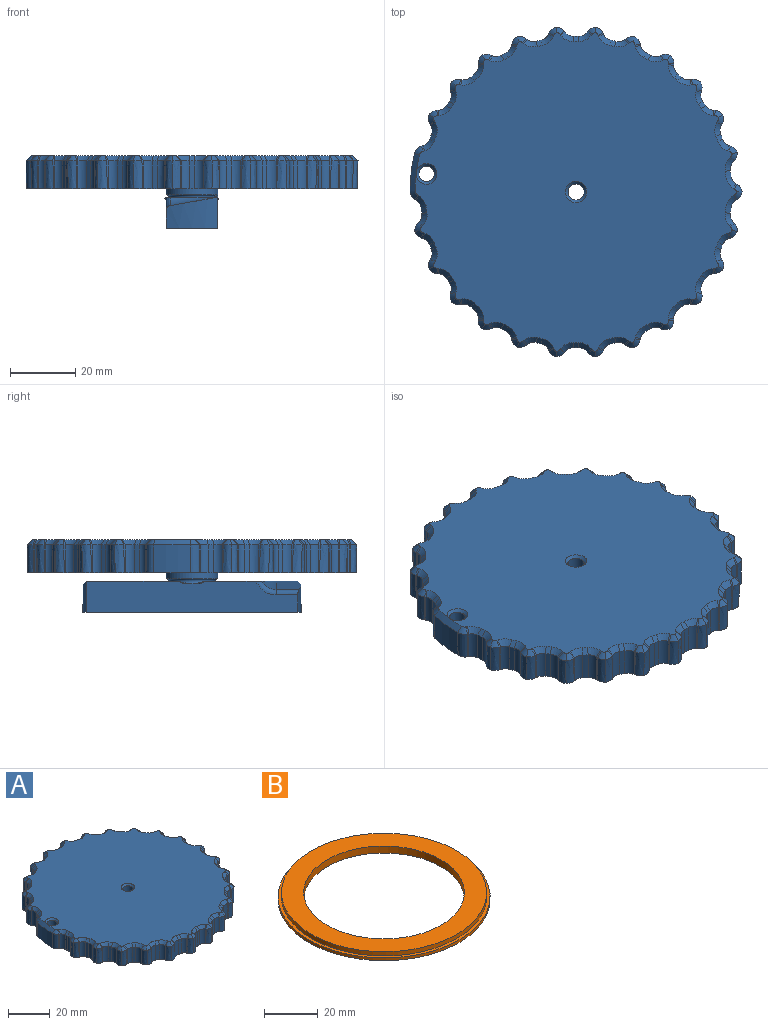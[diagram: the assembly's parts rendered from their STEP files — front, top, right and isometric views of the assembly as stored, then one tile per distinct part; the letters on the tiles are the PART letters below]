
ASSEMBLY  parts=2 mates=1
PART A: 388 faces, bbox 105.4x104.9x57.9 mm
  f0: plane 66.68x15.88mm, normal (0,0,-1), area 971.9mm2, adj f4,f5,f6,f15,f374,f375,f376,f377
  f1: plane 98.34x97.56mm, normal (0,0,1), area 6895.4mm2, adj f195,f196,f197,f198,f199,f200,f201,f202
  f2: cone r=50.8mm half-angle=0.9deg, axis (0,0,1), area 98.1mm2, adj f3,f117,f118,f370
  f3: cone r=50.64mm half-angle=89.1deg, axis (0,0,-1), area 1716.2mm2, adj f2,f13,f20,f21,f22,f23,f24,f25
  f4: cylinder r=33.34mm len=15.88mm, axis (0,0,-1), area 129.3mm2, adj f0,f5,f15,f17,f386
  f5: plane 65.7x10.47mm, normal (-1,0,0), area 566mm2, adj f0,f4,f6,f7,f8,f9,f17,f384
  f6: cylinder r=33.34mm len=15.88mm, axis (0,0,-1), area 129.3mm2, adj f0,f5,f15,f16,f384
  f7: torus R=7.94mm, axis (0,0,-1), area 187.3mm2, adj f5,f8,f9,f12,f15
  f8: plane 25.26x19.05mm, normal (0,0,1), area 240.7mm2, adj f5,f7,f15,f19,f385
  f9: plane 22.28x16.07mm, normal (0,0,1), area 240.7mm2, adj f5,f7,f15,f18,f387
  f10: plane 76.2x76.2mm, normal (0,0,-1), area 4320.9mm2, adj f11,f14
  f11: torus R=7.94mm, axis (0,0,-1), area 182.6mm2, adj f10,f12
  f12: cylinder r=7.94mm len=15.88mm, axis (0,0,-1), area 237.5mm2, adj f7,f11
  f13: cone r=42.86mm half-angle=52.3deg, axis (0,0,-1), area 1227.5mm2, adj f3,f14,f373
  f14: torus R=38.89mm, axis (0,0,-1), area 868.8mm2, adj f10,f13
  f15: plane 67.96x12.72mm, normal (1,0,0), area 566mm2, adj f0,f4,f6,f7,f8,f9,f16,f386
  f16: plane 14.58x7.63mm, normal (-0.17,0,0.98), area 108.6mm2, adj f6,f15,f19,f384
  f17: plane 14.58x7.63mm, normal (0.17,0,0.98), area 108.6mm2, adj f4,f5,f18,f386
  f18: cylinder r=5.08mm len=15mm, axis (0.98,0,-0.17), area 50.6mm2, adj f9,f17,f387
  f19: cylinder r=5.08mm len=15mm, axis (0.98,0,0.17), area 50.6mm2, adj f8,f16,f385
  f20: plane 8.55x0.35mm, normal (0.78,0.62,0), area 3.1mm2, adj f3,f127,f193,f297
  f21: plane 8.55x0.35mm, normal (-0.78,0.62,0), area 3.1mm2, adj f3,f143,f194,f289
  f22: cylinder r=47.62mm len=8.52mm, axis (0,0,1), area 14.2mm2, adj f3,f193,f194,f293
  f23: plane 8.55x0.4mm, normal (0.91,0.41,0), area 3.1mm2, adj f3,f144,f145,f283
  f24: plane 8.55x0.35mm, normal (-0.61,0.79,0), area 3.1mm2, adj f3,f141,f146,f275
  f25: cylinder r=47.62mm len=8.52mm, axis (0,0,1), area 14.2mm2, adj f3,f145,f146,f279
  f26: plane 8.55x0.44mm, normal (0.98,0.18,0), area 3.1mm2, adj f3,f142,f147,f269
  f27: plane 8.55x0.41mm, normal (-0.41,0.91,0), area 3.1mm2, adj f3,f139,f148,f261
  f28: cylinder r=47.62mm len=8.52mm, axis (0,0,1), area 14.2mm2, adj f3,f147,f148,f265
  f29: plane 8.55x0.44mm, normal (1,-0.06,0), area 3.1mm2, adj f3,f140,f149,f255
  f30: plane 8.55x0.44mm, normal (-0.18,0.98,0), area 3.1mm2, adj f3,f137,f150,f247
  f31: cylinder r=47.62mm len=8.52mm, axis (0,0,1), area 14.2mm2, adj f3,f149,f150,f251
  f32: plane 8.55x0.43mm, normal (0.96,-0.29,0), area 3.1mm2, adj f3,f138,f151,f241
  f33: plane 8.55x0.44mm, normal (0.06,1,0), area 3.1mm2, adj f3,f135,f152,f233
  f34: cylinder r=47.62mm len=8.52mm, axis (0,0,1), area 14.2mm2, adj f3,f151,f152,f237
  f35: plane 8.55x0.38mm, normal (0.86,-0.51,0), area 3.1mm2, adj f3,f136,f153,f227
  f36: plane 8.55x0.42mm, normal (0.3,0.95,0), area 3.1mm2, adj f3,f133,f154,f219
  f37: cylinder r=47.62mm len=8.52mm, axis (0,0,1), area 14.2mm2, adj f3,f153,f154,f223
  f38: plane 8.55x0.32mm, normal (0.71,-0.7,0), area 3.1mm2, adj f3,f134,f155,f213
  f39: plane 8.55x0.38mm, normal (0.52,0.85,0), area 3.1mm2, adj f3,f131,f156,f205
  f40: cylinder r=47.62mm len=8.52mm, axis (0,0,1), area 14.2mm2, adj f3,f155,f156,f209
  f41: plane 8.55x0.38mm, normal (0.52,-0.85,0), area 3.1mm2, adj f3,f132,f157,f199
  f42: plane 8.55x0.32mm, normal (0.71,0.7,0), area 3.1mm2, adj f3,f129,f158,f198
  f43: cylinder r=47.62mm len=8.52mm, axis (0,0,1), area 14.2mm2, adj f3,f157,f158,f195
  f44: plane 8.55x0.42mm, normal (0.3,-0.95,0), area 3.1mm2, adj f3,f130,f159,f204
  f45: plane 8.55x0.38mm, normal (0.86,0.51,0), area 3.1mm2, adj f3,f95,f160,f212
  f46: cylinder r=47.62mm len=8.52mm, axis (0,0,1), area 14.2mm2, adj f3,f159,f160,f208
  f47: plane 8.55x0.35mm, normal (0.61,0.79,0), area 3.1mm2, adj f3,f125,f191,f311
  f48: plane 8.55x0.4mm, normal (-0.91,0.41,0), area 3.1mm2, adj f3,f128,f192,f303
  f49: cylinder r=47.62mm len=8.52mm, axis (0,0,1), area 14.2mm2, adj f3,f191,f192,f307
  f50: plane 8.55x0.41mm, normal (0.41,0.91,0), area 3.1mm2, adj f3,f123,f189,f325
  f51: plane 8.55x0.44mm, normal (-0.98,0.18,0), area 3.1mm2, adj f3,f126,f190,f317
  f52: cylinder r=47.62mm len=8.52mm, axis (0,0,1), area 14.2mm2, adj f3,f189,f190,f321
  f53: plane 8.55x0.44mm, normal (0.18,0.98,0), area 3.1mm2, adj f3,f121,f187,f339
  f54: plane 8.55x0.44mm, normal (-1,-0.06,0), area 3.1mm2, adj f3,f124,f188,f331
  f55: cylinder r=47.62mm len=8.52mm, axis (0,0,1), area 14.2mm2, adj f3,f187,f188,f335
  f56: plane 8.55x0.44mm, normal (-0.06,1,0), area 3.1mm2, adj f3,f119,f185,f353
  f57: plane 8.55x0.43mm, normal (-0.96,-0.29,0), area 3.1mm2, adj f3,f122,f186,f345
  f58: cylinder r=47.62mm len=8.52mm, axis (0,0,1), area 14.2mm2, adj f3,f185,f186,f349
  f59: plane 8.55x0.42mm, normal (-0.3,0.95,0), area 3.1mm2, adj f3,f118,f183,f367
  f60: plane 8.55x0.38mm, normal (-0.86,-0.51,0), area 3.1mm2, adj f3,f120,f184,f359
  f61: cylinder r=47.62mm len=8.52mm, axis (0,0,1), area 14.2mm2, adj f3,f183,f184,f363
  f62: plane 8.55x0.32mm, normal (-0.71,0.7,0), area 3.1mm2, adj f3,f115,f181,f358
  f63: plane 8.55x0.38mm, normal (-0.52,-0.85,0), area 3.1mm2, adj f3,f117,f182,f366
  f64: cylinder r=47.62mm len=8.52mm, axis (0,0,1), area 14.2mm2, adj f3,f181,f182,f362
  f65: plane 8.55x0.38mm, normal (-0.86,0.51,0), area 3.1mm2, adj f3,f113,f179,f344
  f66: plane 8.55x0.42mm, normal (-0.3,-0.95,0), area 3.1mm2, adj f3,f116,f180,f352
  f67: cylinder r=47.62mm len=8.52mm, axis (0,0,1), area 14.2mm2, adj f3,f179,f180,f348
  f68: plane 8.55x0.43mm, normal (-0.96,0.29,0), area 3.1mm2, adj f3,f111,f177,f330
  f69: plane 8.55x0.44mm, normal (-0.06,-1,0), area 3.1mm2, adj f3,f114,f178,f338
  f70: cylinder r=47.62mm len=8.52mm, axis (0,0,1), area 14.2mm2, adj f3,f177,f178,f334
  f71: plane 8.55x0.44mm, normal (-1,0.06,0), area 3.1mm2, adj f3,f109,f175,f316
  f72: plane 8.55x0.44mm, normal (0.18,-0.98,0), area 3.1mm2, adj f3,f112,f176,f324
  f73: cylinder r=47.62mm len=8.52mm, axis (0,0,1), area 14.2mm2, adj f3,f175,f176,f320
  f74: plane 8.55x0.44mm, normal (-0.98,-0.18,0), area 3.1mm2, adj f3,f107,f173,f302
  f75: plane 8.55x0.41mm, normal (0.41,-0.91,0), area 3.1mm2, adj f3,f110,f174,f310
  f76: cylinder r=47.62mm len=8.52mm, axis (0,0,1), area 14.2mm2, adj f3,f173,f174,f306
  f77: plane 8.55x0.4mm, normal (-0.91,-0.41,0), area 3.1mm2, adj f3,f105,f171,f288
  f78: plane 8.55x0.35mm, normal (0.61,-0.79,0), area 3.1mm2, adj f3,f108,f172,f296
  f79: cylinder r=47.62mm len=8.52mm, axis (0,0,1), area 14.2mm2, adj f3,f171,f172,f292
  f80: plane 8.55x0.35mm, normal (-0.78,-0.62,0), area 3.1mm2, adj f3,f103,f169,f274
  f81: plane 8.55x0.35mm, normal (0.78,-0.62,0), area 3.1mm2, adj f3,f106,f170,f282
  f82: cylinder r=47.62mm len=8.52mm, axis (0,0,1), area 14.2mm2, adj f3,f169,f170,f278
  f83: plane 8.55x0.35mm, normal (-0.61,-0.79,0), area 3.1mm2, adj f3,f101,f167,f260
  f84: plane 8.55x0.4mm, normal (0.91,-0.41,0), area 3.1mm2, adj f3,f104,f168,f268
  f85: cylinder r=47.62mm len=8.52mm, axis (0,0,1), area 14.2mm2, adj f3,f167,f168,f264
  f86: plane 8.55x0.41mm, normal (-0.41,-0.91,0), area 3.1mm2, adj f3,f99,f165,f246
  f87: plane 8.55x0.44mm, normal (0.98,-0.18,0), area 3.1mm2, adj f3,f102,f166,f254
  f88: cylinder r=47.62mm len=8.52mm, axis (0,0,1), area 14.2mm2, adj f3,f165,f166,f250
  f89: plane 8.55x0.44mm, normal (-0.18,-0.98,0), area 3.1mm2, adj f3,f97,f163,f232
  f90: plane 8.55x0.44mm, normal (1,0.06,0), area 3.1mm2, adj f3,f100,f164,f240
  f91: cylinder r=47.62mm len=8.52mm, axis (0,0,1), area 14.2mm2, adj f3,f163,f164,f236
  f92: plane 8.55x0.44mm, normal (0.06,-1,0), area 3.1mm2, adj f3,f96,f161,f218
  f93: plane 8.55x0.43mm, normal (0.96,0.29,0), area 3.1mm2, adj f3,f98,f162,f226
  f94: cylinder r=47.62mm len=8.52mm, axis (0,0,1), area 14.2mm2, adj f3,f161,f162,f222
  f95: bspline ~43.81x3.82mm, area 24.6mm2, adj f3,f45,f96,f214
  f96: bspline ~43.88x3.42mm, area 24.6mm2, adj f3,f92,f95,f216
  f97: bspline ~43.86x3.75mm, area 24.6mm2, adj f3,f89,f98,f230
  f98: bspline ~43.82x3.83mm, area 24.6mm2, adj f3,f93,f97,f228
  f99: bspline ~43.7x3.85mm, area 24.6mm2, adj f3,f86,f100,f244
  f100: bspline ~43.83x3.61mm, area 24.6mm2, adj f3,f90,f99,f242
  f101: bspline ~43.96x3.74mm, area 24.6mm2, adj f3,f83,f102,f258
  f102: bspline ~43.99x3.18mm, area 24.6mm2, adj f3,f87,f101,f256
  f103: bspline ~44.04x3.41mm, area 24.6mm2, adj f3,f80,f104,f272
  f104: bspline ~44.04x2.88mm, area 24.6mm2, adj f3,f84,f103,f270
  f105: bspline ~44.04x2.88mm, area 24.6mm2, adj f3,f77,f106,f286
  f106: bspline ~44.04x3.41mm, area 24.6mm2, adj f3,f81,f105,f284
  f107: bspline ~43.99x3.18mm, area 24.6mm2, adj f3,f74,f108,f300
  f108: bspline ~43.96x3.74mm, area 24.6mm2, adj f3,f78,f107,f298
  f109: bspline ~43.83x3.61mm, area 24.6mm2, adj f3,f71,f110,f314
  f110: bspline ~43.7x3.85mm, area 24.6mm2, adj f3,f75,f109,f312
  f111: bspline ~43.82x3.83mm, area 24.6mm2, adj f3,f68,f112,f328
  f112: bspline ~43.86x3.75mm, area 24.6mm2, adj f3,f72,f111,f326
  f113: bspline ~43.81x3.82mm, area 24.6mm2, adj f3,f65,f114,f342
  f114: bspline ~43.88x3.42mm, area 24.6mm2, adj f3,f69,f113,f340
  f115: bspline ~44.04x3.6mm, area 24.6mm2, adj f3,f62,f116,f356
  f116: bspline ~44.05x2.9mm, area 24.6mm2, adj f3,f66,f115,f354
  f117: bspline ~54.28x3.27mm, area 28mm2, adj f2,f3,f63,f368
  f118: bspline ~54.74x3.09mm, area 28mm2, adj f2,f3,f59,f369
  f119: bspline ~43.88x3.42mm, area 24.6mm2, adj f3,f56,f120,f355
  f120: bspline ~43.81x3.82mm, area 24.6mm2, adj f3,f60,f119,f357
  f121: bspline ~43.86x3.75mm, area 24.6mm2, adj f3,f53,f122,f341
  f122: bspline ~43.82x3.83mm, area 24.6mm2, adj f3,f57,f121,f343
  f123: bspline ~43.7x3.85mm, area 24.6mm2, adj f3,f50,f124,f327
  f124: bspline ~43.83x3.61mm, area 24.6mm2, adj f3,f54,f123,f329
  f125: bspline ~43.96x3.74mm, area 24.6mm2, adj f3,f47,f126,f313
  f126: bspline ~43.99x3.18mm, area 24.6mm2, adj f3,f51,f125,f315
  f127: bspline ~44.04x3.41mm, area 24.6mm2, adj f3,f20,f128,f299
  f128: bspline ~44.04x2.88mm, area 24.6mm2, adj f3,f48,f127,f301
  f129: bspline ~44.04x3.6mm, area 24.6mm2, adj f3,f42,f130,f200
  f130: bspline ~44.05x2.9mm, area 24.6mm2, adj f3,f44,f129,f202
  f131: bspline ~43.98x3.17mm, area 24.6mm2, adj f3,f39,f132,f203
  f132: bspline ~43.98x3.17mm, area 24.6mm2, adj f3,f41,f131,f201
  f133: bspline ~44.05x2.9mm, area 24.6mm2, adj f3,f36,f134,f217
  f134: bspline ~44.04x3.6mm, area 24.6mm2, adj f3,f38,f133,f215
  f135: bspline ~43.88x3.42mm, area 24.6mm2, adj f3,f33,f136,f231
  f136: bspline ~43.81x3.82mm, area 24.6mm2, adj f3,f35,f135,f229
  f137: bspline ~43.86x3.75mm, area 24.6mm2, adj f3,f30,f138,f245
  f138: bspline ~43.82x3.83mm, area 24.6mm2, adj f3,f32,f137,f243
  f139: bspline ~43.7x3.85mm, area 24.6mm2, adj f3,f27,f140,f259
  f140: bspline ~43.83x3.61mm, area 24.6mm2, adj f3,f29,f139,f257
  f141: bspline ~43.96x3.74mm, area 24.6mm2, adj f3,f24,f142,f273
  f142: bspline ~43.99x3.18mm, area 24.6mm2, adj f3,f26,f141,f271
  f143: bspline ~44.04x3.41mm, area 24.6mm2, adj f3,f21,f144,f287
  f144: bspline ~44.04x2.88mm, area 24.6mm2, adj f3,f23,f143,f285
  f145: cylinder r=3.17mm len=8.54mm, axis (0,0,1), area 24.9mm2, adj f3,f23,f25,f281
  f146: cylinder r=3.17mm len=8.54mm, axis (0,0,1), area 24.9mm2, adj f3,f24,f25,f277
  f147: cylinder r=3.17mm len=8.54mm, axis (0,0,1), area 24.9mm2, adj f3,f26,f28,f267
  f148: cylinder r=3.17mm len=8.54mm, axis (0,0,1), area 24.9mm2, adj f3,f27,f28,f263
  f149: cylinder r=3.17mm len=8.54mm, axis (0,0,1), area 24.9mm2, adj f3,f29,f31,f253
  f150: cylinder r=3.17mm len=8.54mm, axis (0,0,1), area 24.9mm2, adj f3,f30,f31,f249
  f151: cylinder r=3.17mm len=8.54mm, axis (0,0,1), area 24.9mm2, adj f3,f32,f34,f239
  f152: cylinder r=3.17mm len=8.54mm, axis (0,0,1), area 24.9mm2, adj f3,f33,f34,f235
  f153: cylinder r=3.17mm len=8.54mm, axis (0,0,1), area 24.9mm2, adj f3,f35,f37,f225
  f154: cylinder r=3.17mm len=8.54mm, axis (0,0,1), area 24.9mm2, adj f3,f36,f37,f221
  f155: cylinder r=3.17mm len=8.54mm, axis (0,0,1), area 24.9mm2, adj f3,f38,f40,f211
  f156: cylinder r=3.17mm len=8.54mm, axis (0,0,1), area 24.9mm2, adj f3,f39,f40,f207
  f157: cylinder r=3.17mm len=8.54mm, axis (0,0,1), area 24.9mm2, adj f3,f41,f43,f197
  f158: cylinder r=3.17mm len=8.54mm, axis (0,0,1), area 24.9mm2, adj f3,f42,f43,f196
  f159: cylinder r=3.17mm len=8.54mm, axis (0,0,1), area 24.9mm2, adj f3,f44,f46,f206
  f160: cylinder r=3.17mm len=8.54mm, axis (0,0,1), area 24.9mm2, adj f3,f45,f46,f210
  f161: cylinder r=3.17mm len=8.54mm, axis (0,0,1), area 24.9mm2, adj f3,f92,f94,f220
  f162: cylinder r=3.17mm len=8.54mm, axis (0,0,1), area 24.9mm2, adj f3,f93,f94,f224
  f163: cylinder r=3.17mm len=8.54mm, axis (0,0,1), area 24.9mm2, adj f3,f89,f91,f234
  f164: cylinder r=3.17mm len=8.54mm, axis (0,0,1), area 24.9mm2, adj f3,f90,f91,f238
  f165: cylinder r=3.17mm len=8.54mm, axis (0,0,1), area 24.9mm2, adj f3,f86,f88,f248
  f166: cylinder r=3.17mm len=8.54mm, axis (0,0,1), area 24.9mm2, adj f3,f87,f88,f252
  f167: cylinder r=3.17mm len=8.54mm, axis (0,0,1), area 24.9mm2, adj f3,f83,f85,f262
  f168: cylinder r=3.17mm len=8.54mm, axis (0,0,1), area 24.9mm2, adj f3,f84,f85,f266
  f169: cylinder r=3.17mm len=8.54mm, axis (0,0,1), area 24.9mm2, adj f3,f80,f82,f276
  f170: cylinder r=3.17mm len=8.54mm, axis (0,0,1), area 24.9mm2, adj f3,f81,f82,f280
  f171: cylinder r=3.17mm len=8.54mm, axis (0,0,1), area 24.9mm2, adj f3,f77,f79,f290
  f172: cylinder r=3.17mm len=8.54mm, axis (0,0,1), area 24.9mm2, adj f3,f78,f79,f294
  f173: cylinder r=3.17mm len=8.54mm, axis (0,0,1), area 24.9mm2, adj f3,f74,f76,f304
  f174: cylinder r=3.17mm len=8.54mm, axis (0,0,1), area 24.9mm2, adj f3,f75,f76,f308
  f175: cylinder r=3.17mm len=8.54mm, axis (0,0,1), area 24.9mm2, adj f3,f71,f73,f318
  f176: cylinder r=3.17mm len=8.54mm, axis (0,0,1), area 24.9mm2, adj f3,f72,f73,f322
  f177: cylinder r=3.17mm len=8.54mm, axis (0,0,1), area 24.9mm2, adj f3,f68,f70,f332
  f178: cylinder r=3.17mm len=8.54mm, axis (0,0,1), area 24.9mm2, adj f3,f69,f70,f336
  f179: cylinder r=3.17mm len=8.54mm, axis (0,0,1), area 24.9mm2, adj f3,f65,f67,f346
  f180: cylinder r=3.17mm len=8.54mm, axis (0,0,1), area 24.9mm2, adj f3,f66,f67,f350
  f181: cylinder r=3.17mm len=8.54mm, axis (0,0,1), area 24.9mm2, adj f3,f62,f64,f360
  f182: cylinder r=3.17mm len=8.54mm, axis (0,0,1), area 24.9mm2, adj f3,f63,f64,f364
  f183: cylinder r=3.17mm len=8.54mm, axis (0,0,1), area 24.9mm2, adj f3,f59,f61,f365
  f184: cylinder r=3.17mm len=8.54mm, axis (0,0,1), area 24.9mm2, adj f3,f60,f61,f361
  f185: cylinder r=3.17mm len=8.54mm, axis (0,0,1), area 24.9mm2, adj f3,f56,f58,f351
  f186: cylinder r=3.17mm len=8.54mm, axis (0,0,1), area 24.9mm2, adj f3,f57,f58,f347
  f187: cylinder r=3.17mm len=8.54mm, axis (0,0,1), area 24.9mm2, adj f3,f53,f55,f337
  f188: cylinder r=3.17mm len=8.54mm, axis (0,0,1), area 24.9mm2, adj f3,f54,f55,f333
  f189: cylinder r=3.17mm len=8.54mm, axis (0,0,1), area 24.9mm2, adj f3,f50,f52,f323
  f190: cylinder r=3.17mm len=8.54mm, axis (0,0,1), area 24.9mm2, adj f3,f51,f52,f319
  f191: cylinder r=3.17mm len=8.54mm, axis (0,0,1), area 24.9mm2, adj f3,f47,f49,f309
  f192: cylinder r=3.17mm len=8.54mm, axis (0,0,1), area 24.9mm2, adj f3,f48,f49,f305
  f193: cylinder r=3.17mm len=8.54mm, axis (0,0,1), area 24.9mm2, adj f3,f20,f22,f295
  f194: cylinder r=3.17mm len=8.54mm, axis (0,0,1), area 24.9mm2, adj f3,f21,f22,f291
  f195: cone r=46.04mm half-angle=45deg, axis (0,0,-1), area 3.7mm2, adj f1,f43,f196,f197
  f196: cone r=4.76mm half-angle=45deg, axis (0,0,1), area 8.2mm2, adj f1,f158,f195,f198
  f197: cone r=4.76mm half-angle=45deg, axis (0,0,1), area 8.2mm2, adj f1,f157,f195,f199
  f198: plane 1.59x1.44mm, normal (0.5,0.5,0.71), area 1mm2, adj f1,f42,f196,f200
  f199: plane 1.59x1.59mm, normal (0.37,-0.6,0.71), area 1mm2, adj f1,f41,f197,f201
  f200: bspline ~2.76x2.18mm, area 4.5mm2, adj f1,f129,f198,f202
  f201: bspline ~2.59x2.34mm, area 4.5mm2, adj f1,f132,f199,f203
  f202: bspline ~2.48x2.45mm, area 4.5mm2, adj f1,f130,f200,f204
  f203: bspline ~2.59x2.34mm, area 4.5mm2, adj f1,f131,f201,f205
  f204: plane 1.65x1.59mm, normal (0.21,-0.67,0.71), area 1mm2, adj f1,f44,f202,f206
  f205: plane 1.59x1.59mm, normal (0.37,0.6,0.71), area 1mm2, adj f1,f39,f203,f207
  f206: cone r=4.76mm half-angle=45deg, axis (0,0,1), area 8.2mm2, adj f1,f159,f204,f208
  f207: cone r=4.76mm half-angle=45deg, axis (0,0,1), area 8.2mm2, adj f1,f156,f205,f209
  f208: cone r=46.04mm half-angle=45deg, axis (0,0,-1), area 3.7mm2, adj f1,f46,f206,f210
  f209: cone r=46.04mm half-angle=45deg, axis (0,0,-1), area 3.7mm2, adj f1,f40,f207,f211
  f210: cone r=4.76mm half-angle=45deg, axis (0,0,1), area 8.2mm2, adj f1,f160,f208,f212
  f211: cone r=4.76mm half-angle=45deg, axis (0,0,1), area 8.2mm2, adj f1,f155,f209,f213
  f212: plane 1.59x1.59mm, normal (0.61,0.36,0.71), area 1mm2, adj f1,f45,f210,f214
  f213: plane 1.59x1.44mm, normal (0.5,-0.5,0.71), area 1mm2, adj f1,f38,f211,f215
  f214: bspline ~2.89x1.96mm, area 4.5mm2, adj f1,f95,f212,f216
  f215: bspline ~2.76x2.18mm, area 4.5mm2, adj f1,f134,f213,f217
  f216: bspline ~2.59x2.32mm, area 4.5mm2, adj f1,f96,f214,f218
  f217: bspline ~2.48x2.45mm, area 4.5mm2, adj f1,f133,f215,f219
  f218: plane 1.61x1.59mm, normal (0.05,-0.71,0.71), area 1mm2, adj f1,f92,f216,f220
  f219: plane 1.65x1.59mm, normal (0.21,0.67,0.71), area 1mm2, adj f1,f36,f217,f221
  f220: cone r=4.76mm half-angle=45deg, axis (0,0,1), area 8.2mm2, adj f1,f161,f218,f222
  f221: cone r=4.76mm half-angle=45deg, axis (0,0,1), area 8.2mm2, adj f1,f154,f219,f223
  f222: cone r=46.04mm half-angle=45deg, axis (0,0,-1), area 3.7mm2, adj f1,f94,f220,f224
  f223: cone r=46.04mm half-angle=45deg, axis (0,0,-1), area 3.7mm2, adj f1,f37,f221,f225
  f224: cone r=4.76mm half-angle=45deg, axis (0,0,1), area 8.2mm2, adj f1,f162,f222,f226
  f225: cone r=4.76mm half-angle=45deg, axis (0,0,1), area 8.2mm2, adj f1,f153,f223,f227
  f226: plane 1.65x1.59mm, normal (0.68,0.21,0.71), area 1mm2, adj f1,f93,f224,f228
  f227: plane 1.59x1.59mm, normal (0.61,-0.36,0.71), area 1mm2, adj f1,f35,f225,f229
  f228: bspline ~2.85x2.07mm, area 4.5mm2, adj f1,f98,f226,f230
  f229: bspline ~2.89x1.96mm, area 4.5mm2, adj f1,f136,f227,f231
  f230: bspline ~2.77x2.17mm, area 4.5mm2, adj f1,f97,f228,f232
  f231: bspline ~2.59x2.32mm, area 4.5mm2, adj f1,f135,f229,f233
  f232: plane 1.64x1.59mm, normal (-0.12,-0.7,0.71), area 1mm2, adj f1,f89,f230,f234
  f233: plane 1.61x1.59mm, normal (0.05,0.71,0.71), area 1mm2, adj f1,f33,f231,f235
  f234: cone r=4.76mm half-angle=45deg, axis (0,0,1), area 8.2mm2, adj f1,f163,f232,f236
  f235: cone r=4.76mm half-angle=45deg, axis (0,0,1), area 8.2mm2, adj f1,f152,f233,f237
  f236: cone r=46.04mm half-angle=45deg, axis (0,0,-1), area 3.7mm2, adj f1,f91,f234,f238
  f237: cone r=46.04mm half-angle=45deg, axis (0,0,-1), area 3.7mm2, adj f1,f34,f235,f239
  f238: cone r=4.76mm half-angle=45deg, axis (0,0,1), area 8.2mm2, adj f1,f164,f236,f240
  f239: cone r=4.76mm half-angle=45deg, axis (0,0,1), area 8.2mm2, adj f1,f151,f237,f241
  f240: plane 1.61x1.59mm, normal (0.71,0.04,0.71), area 1mm2, adj f1,f90,f238,f242
  f241: plane 1.65x1.59mm, normal (0.68,-0.21,0.71), area 1mm2, adj f1,f32,f239,f243
  f242: bspline ~2.54x2.11mm, area 4.5mm2, adj f1,f100,f240,f244
  f243: bspline ~2.85x2.07mm, area 4.5mm2, adj f1,f138,f241,f245
  f244: bspline ~2.89x1.94mm, area 4.5mm2, adj f1,f99,f242,f246
  f245: bspline ~2.65x1.98mm, area 4.5mm2, adj f1,f137,f243,f247
  f246: plane 1.63x1.59mm, normal (-0.29,-0.65,0.71), area 1mm2, adj f1,f86,f244,f248
  f247: plane 1.64x1.59mm, normal (-0.12,0.7,0.71), area 1mm2, adj f1,f30,f245,f249
  f248: cone r=4.76mm half-angle=45deg, axis (0,0,1), area 8.2mm2, adj f1,f165,f246,f250
  f249: cone r=4.76mm half-angle=45deg, axis (0,0,1), area 8.2mm2, adj f1,f150,f247,f251
  f250: cone r=46.04mm half-angle=45deg, axis (0,0,-1), area 3.7mm2, adj f1,f88,f248,f252
  f251: cone r=46.04mm half-angle=45deg, axis (0,0,-1), area 3.7mm2, adj f1,f31,f249,f253
  f252: cone r=4.76mm half-angle=45deg, axis (0,0,1), area 8.2mm2, adj f1,f166,f250,f254
  f253: cone r=4.76mm half-angle=45deg, axis (0,0,1), area 8.2mm2, adj f1,f149,f251,f255
  f254: plane 1.64x1.59mm, normal (0.69,-0.13,0.71), area 1mm2, adj f1,f87,f252,f256
  f255: plane 1.61x1.59mm, normal (0.71,-0.04,0.71), area 1mm2, adj f1,f29,f253,f257
  f256: bspline ~2.58x2.45mm, area 4.5mm2, adj f1,f102,f254,f258
  f257: bspline ~2.64x2.23mm, area 4.5mm2, adj f1,f140,f255,f259
  f258: bspline ~2.84x2.08mm, area 4.5mm2, adj f1,f101,f256,f260
  f259: bspline ~2.89x1.94mm, area 4.5mm2, adj f1,f139,f257,f261
  f260: plane 1.59x1.53mm, normal (-0.43,-0.56,0.71), area 1mm2, adj f1,f83,f258,f262
  f261: plane 1.63x1.59mm, normal (-0.29,0.65,0.71), area 1mm2, adj f1,f27,f259,f263
  f262: cone r=4.76mm half-angle=45deg, axis (0,0,1), area 8.2mm2, adj f1,f167,f260,f264
  f263: cone r=4.76mm half-angle=45deg, axis (0,0,1), area 8.2mm2, adj f1,f148,f261,f265
  f264: cone r=46.04mm half-angle=45deg, axis (0,0,-1), area 3.7mm2, adj f1,f85,f262,f266
  f265: cone r=46.04mm half-angle=45deg, axis (0,0,-1), area 3.7mm2, adj f1,f28,f263,f267
  f266: cone r=4.76mm half-angle=45deg, axis (0,0,1), area 8.2mm2, adj f1,f168,f264,f268
  f267: cone r=4.76mm half-angle=45deg, axis (0,0,1), area 8.2mm2, adj f1,f147,f265,f269
  f268: plane 1.63x1.59mm, normal (0.64,-0.29,0.71), area 1mm2, adj f1,f84,f266,f270
  f269: plane 1.64x1.59mm, normal (0.69,0.13,0.71), area 1mm2, adj f1,f26,f267,f271
  f270: bspline ~2.58x2.46mm, area 4.5mm2, adj f1,f104,f268,f272
  f271: bspline ~2.58x2.45mm, area 4.5mm2, adj f1,f142,f269,f273
  f272: bspline ~2.63x2.24mm, area 4.5mm2, adj f1,f103,f270,f274
  f273: bspline ~2.68x1.92mm, area 4.5mm2, adj f1,f141,f271,f275
  f274: plane 1.59x1.52mm, normal (-0.55,-0.44,0.71), area 1mm2, adj f1,f80,f272,f276
  f275: plane 1.59x1.53mm, normal (-0.43,0.56,0.71), area 1mm2, adj f1,f24,f273,f277
  f276: cone r=4.76mm half-angle=45deg, axis (0,0,1), area 8.2mm2, adj f1,f169,f274,f278
  f277: cone r=4.76mm half-angle=45deg, axis (0,0,1), area 8.2mm2, adj f1,f146,f275,f279
  f278: cone r=46.04mm half-angle=45deg, axis (0,0,-1), area 3.7mm2, adj f1,f82,f276,f280
  f279: cone r=46.04mm half-angle=45deg, axis (0,0,-1), area 3.7mm2, adj f1,f25,f277,f281
  f280: cone r=4.76mm half-angle=45deg, axis (0,0,1), area 8.2mm2, adj f1,f170,f278,f282
  f281: cone r=4.76mm half-angle=45deg, axis (0,0,1), area 8.2mm2, adj f1,f145,f279,f283
  f282: plane 1.59x1.52mm, normal (0.55,-0.44,0.71), area 1mm2, adj f1,f81,f280,f284
  f283: plane 1.63x1.59mm, normal (0.64,0.29,0.71), area 1mm2, adj f1,f23,f281,f285
  f284: bspline ~2.63x2.24mm, area 4.5mm2, adj f1,f106,f282,f286
  f285: bspline ~2.58x2.46mm, area 4.5mm2, adj f1,f144,f283,f287
  f286: bspline ~2.5x2.42mm, area 4.5mm2, adj f1,f105,f284,f288
  f287: bspline ~2.63x2.24mm, area 4.5mm2, adj f1,f143,f285,f289
  f288: plane 1.63x1.59mm, normal (-0.64,-0.29,0.71), area 1mm2, adj f1,f77,f286,f290
  f289: plane 1.59x1.52mm, normal (-0.55,0.44,0.71), area 1mm2, adj f1,f21,f287,f291
  f290: cone r=4.76mm half-angle=45deg, axis (0,0,1), area 8.2mm2, adj f1,f171,f288,f292
  f291: cone r=4.76mm half-angle=45deg, axis (0,0,1), area 8.2mm2, adj f1,f194,f289,f293
  f292: cone r=46.04mm half-angle=45deg, axis (0,0,-1), area 3.7mm2, adj f1,f79,f290,f294
  f293: cone r=46.04mm half-angle=45deg, axis (0,0,-1), area 3.7mm2, adj f1,f22,f291,f295
  f294: cone r=4.76mm half-angle=45deg, axis (0,0,1), area 8.2mm2, adj f1,f172,f292,f296
  f295: cone r=4.76mm half-angle=45deg, axis (0,0,1), area 8.2mm2, adj f1,f193,f293,f297
  f296: plane 1.59x1.53mm, normal (0.43,-0.56,0.71), area 1mm2, adj f1,f78,f294,f298
  f297: plane 1.59x1.52mm, normal (0.55,0.44,0.71), area 1mm2, adj f1,f20,f295,f299
  f298: bspline ~2.68x1.92mm, area 4.5mm2, adj f1,f108,f296,f300
  f299: bspline ~2.63x2.24mm, area 4.5mm2, adj f1,f127,f297,f301
  f300: bspline ~2.58x2.45mm, area 4.5mm2, adj f1,f107,f298,f302
  f301: bspline ~2.58x2.46mm, area 4.5mm2, adj f1,f128,f299,f303
  f302: plane 1.64x1.59mm, normal (-0.69,-0.13,0.71), area 1mm2, adj f1,f74,f300,f304
  f303: plane 1.63x1.59mm, normal (-0.64,0.29,0.71), area 1mm2, adj f1,f48,f301,f305
  f304: cone r=4.76mm half-angle=45deg, axis (0,0,1), area 8.2mm2, adj f1,f173,f302,f306
  f305: cone r=4.76mm half-angle=45deg, axis (0,0,1), area 8.2mm2, adj f1,f192,f303,f307
  f306: cone r=46.04mm half-angle=45deg, axis (0,0,-1), area 3.7mm2, adj f1,f76,f304,f308
  f307: cone r=46.04mm half-angle=45deg, axis (0,0,-1), area 3.7mm2, adj f1,f49,f305,f309
  f308: cone r=4.76mm half-angle=45deg, axis (0,0,1), area 8.2mm2, adj f1,f174,f306,f310
  f309: cone r=4.76mm half-angle=45deg, axis (0,0,1), area 8.2mm2, adj f1,f191,f307,f311
  f310: plane 1.63x1.59mm, normal (0.29,-0.65,0.71), area 1mm2, adj f1,f75,f308,f312
  f311: plane 1.59x1.53mm, normal (0.43,0.56,0.71), area 1mm2, adj f1,f47,f309,f313
  f312: bspline ~2.89x1.94mm, area 4.5mm2, adj f1,f110,f310,f314
  f313: bspline ~2.84x2.08mm, area 4.5mm2, adj f1,f125,f311,f315
  f314: bspline ~2.64x2.23mm, area 4.5mm2, adj f1,f109,f312,f316
  f315: bspline ~2.51x2.37mm, area 4.5mm2, adj f1,f126,f313,f317
  f316: plane 1.61x1.59mm, normal (-0.71,0.04,0.71), area 1mm2, adj f1,f71,f314,f318
  f317: plane 1.64x1.59mm, normal (-0.69,0.13,0.71), area 1mm2, adj f1,f51,f315,f319
  f318: cone r=4.76mm half-angle=45deg, axis (0,0,1), area 8.2mm2, adj f1,f175,f316,f320
  f319: cone r=4.76mm half-angle=45deg, axis (0,0,1), area 8.2mm2, adj f1,f190,f317,f321
  f320: cone r=46.04mm half-angle=45deg, axis (0,0,-1), area 3.7mm2, adj f1,f73,f318,f322
  f321: cone r=46.04mm half-angle=45deg, axis (0,0,-1), area 3.7mm2, adj f1,f52,f319,f323
  f322: cone r=4.76mm half-angle=45deg, axis (0,0,1), area 8.2mm2, adj f1,f176,f320,f324
  f323: cone r=4.76mm half-angle=45deg, axis (0,0,1), area 8.2mm2, adj f1,f189,f321,f325
  f324: plane 1.64x1.59mm, normal (0.12,-0.7,0.71), area 1mm2, adj f1,f72,f322,f326
  f325: plane 1.63x1.59mm, normal (0.29,0.65,0.71), area 1mm2, adj f1,f50,f323,f327
  f326: bspline ~2.65x1.98mm, area 4.5mm2, adj f1,f112,f324,f328
  f327: bspline ~2.89x1.94mm, area 4.5mm2, adj f1,f123,f325,f329
  f328: bspline ~2.71x1.86mm, area 4.5mm2, adj f1,f111,f326,f330
  f329: bspline ~2.54x2.11mm, area 4.5mm2, adj f1,f124,f327,f331
  f330: plane 1.65x1.59mm, normal (-0.68,0.21,0.71), area 1mm2, adj f1,f68,f328,f332
  f331: plane 1.61x1.59mm, normal (-0.71,-0.04,0.71), area 1mm2, adj f1,f54,f329,f333
  f332: cone r=4.76mm half-angle=45deg, axis (0,0,1), area 8.2mm2, adj f1,f177,f330,f334
  f333: cone r=4.76mm half-angle=45deg, axis (0,0,1), area 8.2mm2, adj f1,f188,f331,f335
  f334: cone r=46.04mm half-angle=45deg, axis (0,0,-1), area 3.7mm2, adj f1,f70,f332,f336
  f335: cone r=46.04mm half-angle=45deg, axis (0,0,-1), area 3.7mm2, adj f1,f55,f333,f337
  f336: cone r=4.76mm half-angle=45deg, axis (0,0,1), area 8.2mm2, adj f1,f178,f334,f338
  f337: cone r=4.76mm half-angle=45deg, axis (0,0,1), area 8.2mm2, adj f1,f187,f335,f339
  f338: plane 1.61x1.59mm, normal (-0.05,-0.71,0.71), area 1mm2, adj f1,f69,f336,f340
  f339: plane 1.64x1.59mm, normal (0.12,0.7,0.71), area 1mm2, adj f1,f53,f337,f341
  f340: bspline ~2.59x2.32mm, area 4.5mm2, adj f1,f114,f338,f342
  f341: bspline ~2.77x2.17mm, area 4.5mm2, adj f1,f121,f339,f343
  f342: bspline ~2.89x1.96mm, area 4.5mm2, adj f1,f113,f340,f344
  f343: bspline ~2.85x2.07mm, area 4.5mm2, adj f1,f122,f341,f345
  f344: plane 1.59x1.59mm, normal (-0.61,0.36,0.71), area 1mm2, adj f1,f65,f342,f346
  f345: plane 1.65x1.59mm, normal (-0.68,-0.21,0.71), area 1mm2, adj f1,f57,f343,f347
  f346: cone r=4.76mm half-angle=45deg, axis (0,0,1), area 8.2mm2, adj f1,f179,f344,f348
  f347: cone r=4.76mm half-angle=45deg, axis (0,0,1), area 8.2mm2, adj f1,f186,f345,f349
  f348: cone r=46.04mm half-angle=45deg, axis (0,0,-1), area 3.7mm2, adj f1,f67,f346,f350
  f349: cone r=46.04mm half-angle=45deg, axis (0,0,-1), area 3.7mm2, adj f1,f58,f347,f351
  f350: cone r=4.76mm half-angle=45deg, axis (0,0,1), area 8.2mm2, adj f1,f180,f348,f352
  f351: cone r=4.76mm half-angle=45deg, axis (0,0,1), area 8.2mm2, adj f1,f185,f349,f353
  f352: plane 1.65x1.59mm, normal (-0.21,-0.67,0.71), area 1mm2, adj f1,f66,f350,f354
  f353: plane 1.61x1.59mm, normal (-0.05,0.71,0.71), area 1mm2, adj f1,f56,f351,f355
  f354: bspline ~2.54x2.53mm, area 4.5mm2, adj f1,f116,f352,f356
  f355: bspline ~2.59x2.32mm, area 4.5mm2, adj f1,f119,f353,f357
  f356: bspline ~2.76x2.18mm, area 4.5mm2, adj f1,f115,f354,f358
  f357: bspline ~2.89x1.96mm, area 4.5mm2, adj f1,f120,f355,f359
  f358: plane 1.59x1.44mm, normal (-0.5,0.5,0.71), area 1mm2, adj f1,f62,f356,f360
  f359: plane 1.59x1.59mm, normal (-0.61,-0.36,0.71), area 1mm2, adj f1,f60,f357,f361
  f360: cone r=4.76mm half-angle=45deg, axis (0,0,1), area 8.2mm2, adj f1,f181,f358,f362
  f361: cone r=4.76mm half-angle=45deg, axis (0,0,1), area 8.2mm2, adj f1,f184,f359,f363
  f362: cone r=46.04mm half-angle=45deg, axis (0,0,-1), area 3.7mm2, adj f1,f64,f360,f364
  f363: cone r=46.04mm half-angle=45deg, axis (0,0,-1), area 3.7mm2, adj f1,f61,f361,f365
  f364: cone r=4.76mm half-angle=45deg, axis (0,0,1), area 8.2mm2, adj f1,f182,f362,f366
  f365: cone r=4.76mm half-angle=45deg, axis (0,0,1), area 8.2mm2, adj f1,f183,f363,f367
  f366: plane 1.59x1.59mm, normal (-0.37,-0.6,0.71), area 1mm2, adj f1,f63,f364,f368
  f367: plane 1.65x1.59mm, normal (-0.21,0.67,0.71), area 1mm2, adj f1,f59,f365,f369
  f368: bspline ~2.74x2.37mm, area 5.5mm2, adj f1,f117,f366,f370
  f369: bspline ~2.66x2.61mm, area 5.5mm2, adj f1,f118,f367,f370
  f370: cone r=50.77mm half-angle=44.6deg, axis (0,0,-1), area 25.4mm2, adj f1,f2,f368,f369,f372
  f371: cylinder r=2.38mm len=8.52mm, axis (0,0,1), area 127.4mm2, adj f372,f373
  f372: cone r=2.38mm half-angle=45deg, axis (0,0,1), area 19.8mm2, adj f1,f370,f371
  f373: bspline ~6.36x6.36mm, area 19.8mm2, adj f3,f13,f371
  f374: plane 7.62x4.7mm, normal (0.5,-0.87,0), area 41.3mm2, adj f0,f375,f379,f380
  f375: plane 7.62x4.7mm, normal (-0.5,-0.87,0), area 41.3mm2, adj f0,f374,f376,f380
  f376: plane 7.62x5.43mm, normal (-1,0,0), area 41.3mm2, adj f0,f375,f377,f380
  f377: plane 7.62x4.7mm, normal (-0.5,0.87,0), area 41.3mm2, adj f0,f376,f378,f380
  f378: plane 7.62x4.7mm, normal (0.5,0.87,0), area 41.3mm2, adj f0,f377,f379,f380
  f379: plane 7.62x5.43mm, normal (1,0,0), area 41.3mm2, adj f0,f374,f378,f380
  f380: plane 10.85x9.4mm, normal (0,0,-1), area 42.9mm2, adj f374,f375,f376,f377,f378,f379,f382
  f381: cylinder r=2.48mm len=13.02mm, axis (0,0,-1), area 202.6mm2, adj f382,f383
  f382: cone r=2.48mm half-angle=45deg, axis (0,0,-1), area 20.3mm2, adj f380,f381
  f383: cone r=3.27mm half-angle=45deg, axis (0,0,1), area 20.3mm2, adj f1,f381
  f384: cylinder r=1.59mm len=6.96mm, axis (0,-1,0), area 15.1mm2, adj f5,f6,f16,f385
  f385: bspline ~6.14x4.74mm, area 14.4mm2, adj f5,f8,f19,f384
  f386: cylinder r=1.59mm len=6.96mm, axis (0,-1,0), area 15.1mm2, adj f4,f15,f17,f387
  f387: bspline ~6.14x4.74mm, area 14.4mm2, adj f9,f15,f18,f386
PART B: 6 faces, bbox 78.7x78.7x3.2 mm
  f0: cylinder r=29.84mm len=59.69mm, axis (0,0,1), area 595.4mm2, adj f1,f5
  f1: plane 76.2x76.2mm, normal (0,0,1), area 1762.1mm2, adj f0,f2
  f2: cylinder r=38.1mm len=76.2mm, axis (0,0,1), area 456mm2, adj f1,f3
  f3: plane 78.74x78.74mm, normal (0,0,1), area 309.1mm2, adj f2,f4
  f4: cylinder r=39.37mm len=78.74mm, axis (0,0,1), area 314.2mm2, adj f3,f5
  f5: plane 78.74x78.74mm, normal (0,0,-1), area 2071.2mm2, adj f0,f4
PLACE A t=(-1.1,-8.51,-2.64)mm
PLACE B t=(-1.1,-8.51,-6.58)mm
MATE fastened B.f0 <-> A.f2  axis (0,0,-1) through (-1.1,-8.51,-9.76)mm
